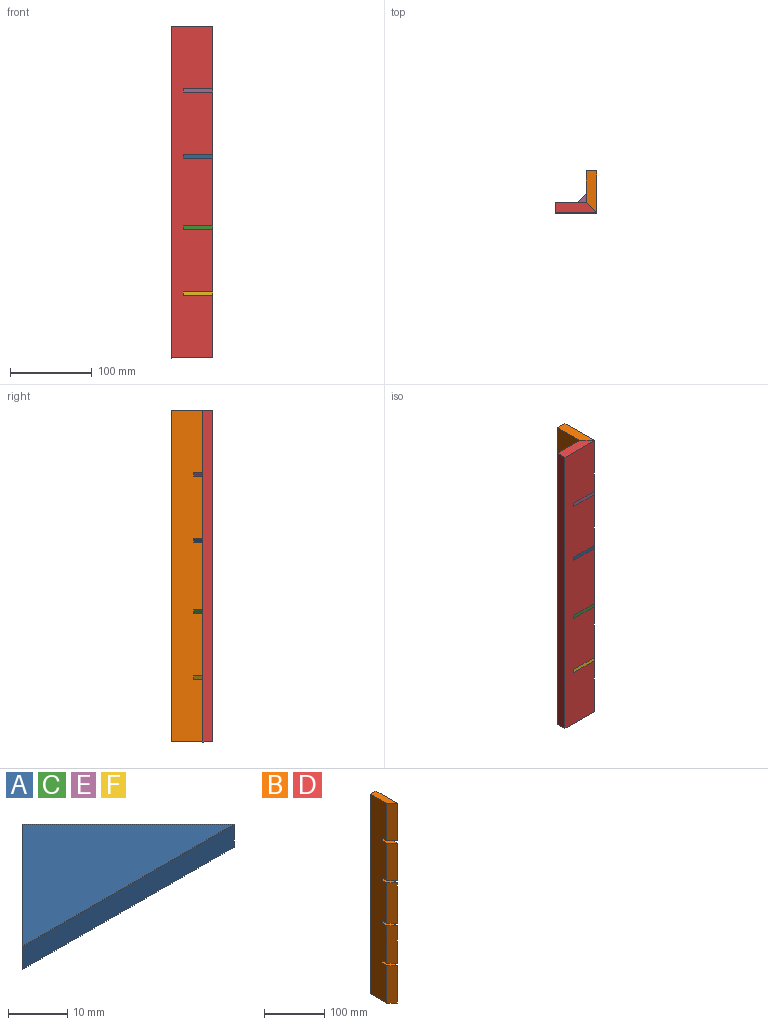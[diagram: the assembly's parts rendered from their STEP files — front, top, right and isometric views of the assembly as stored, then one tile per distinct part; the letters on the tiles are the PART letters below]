
ASSEMBLY  parts=6 mates=8
PART A: 5 faces, bbox 50.8x25.4x4.8 mm
  f0: plane 25.4x25.4mm, normal (-0.71,0.71,0), area 171.1mm2, adj f1,f2,f3,f4
  f1: plane 50.8x4.76mm, normal (0,-1,0), area 241.9mm2, adj f0,f2,f3,f4
  f2: plane 25.4x25.4mm, normal (0.71,0.71,0), area 171.1mm2, adj f0,f1,f3,f4
  f3: plane 50.8x25.4mm, normal (0,0,1), area 645.2mm2, adj f0,f1,f2
  f4: plane 50.8x25.4mm, normal (0,0,-1), area 645.2mm2, adj f0,f1,f2
PART B: 22 faces, bbox 12.7x50.8x406.4 mm
  f0: plane 76.2x12.7mm, normal (-0.71,-0.71,0), area 1368.6mm2, adj f4,f5,f8,f19
  f1: plane 76.2x12.7mm, normal (-0.71,-0.71,0), area 1368.6mm2, adj f4,f5,f15,f16
  f2: plane 76.2x12.7mm, normal (-0.71,-0.71,0), area 1368.6mm2, adj f4,f5,f9,f18
  f3: plane 82.55x12.7mm, normal (-0.71,-0.71,0), area 1482.6mm2, adj f4,f5,f11,f13
  f4: plane 406.4x50.8mm, normal (1,0,0), area 19960.8mm2, adj f0,f1,f2,f3,f6,f7,f8,f9
  f5: plane 406.4x38.1mm, normal (-1,0,0), area 15283.4mm2, adj f0,f1,f2,f3,f6,f7,f8,f9
  f6: plane 76.2x12.7mm, normal (-0.71,-0.71,0), area 1368.6mm2, adj f4,f5,f12,f21
  f7: plane 406.4x12.7mm, normal (0,1,0), area 5161.3mm2, adj f4,f5,f8,f9
  f8: plane 50.8x12.7mm, normal (0,0,1), area 564.5mm2, adj f0,f4,f5,f7
  f9: plane 50.8x12.7mm, normal (0,0,-1), area 564.5mm2, adj f2,f4,f5,f7
  f10: plane 12.7x12.7mm, normal (0.71,-0.71,0), area 85.5mm2, adj f4,f5,f11,f12
  f11: plane 35.92x12.7mm, normal (0,0,1), area 294.9mm2, adj f3,f4,f5,f10
  f12: plane 35.92x12.7mm, normal (0,0,-1), area 294.9mm2, adj f4,f5,f6,f10
  f13: plane 35.92x12.7mm, normal (0,0,-1), area 294.9mm2, adj f3,f4,f5,f14
  f14: plane 12.7x12.7mm, normal (0.71,-0.71,0), area 85.5mm2, adj f4,f5,f13,f15
  f15: plane 35.92x12.7mm, normal (0,0,1), area 294.9mm2, adj f1,f4,f5,f14
  f16: plane 35.92x12.7mm, normal (0,0,-1), area 294.9mm2, adj f1,f4,f5,f17
  f17: plane 12.7x12.7mm, normal (0.71,-0.71,0), area 85.5mm2, adj f4,f5,f16,f18
  f18: plane 35.92x12.7mm, normal (0,0,1), area 294.9mm2, adj f2,f4,f5,f17
  f19: plane 35.92x12.7mm, normal (0,0,-1), area 294.9mm2, adj f0,f4,f5,f20
  f20: plane 12.7x12.7mm, normal (0.71,-0.71,0), area 85.5mm2, adj f4,f5,f19,f21
  f21: plane 35.92x12.7mm, normal (0,0,1), area 294.9mm2, adj f4,f5,f6,f20
PART C: same geometry as A
PART D: same geometry as B
PART E: same geometry as A
PART F: same geometry as A
PLACE A rot(axis=(0.92,0.38,0),180deg) t=(-85.8,196.85,252.71)mm
PLACE B t=(-67.84,178.89,-47.33)mm
PLACE C rot(axis=(0.92,0.38,0),180deg) t=(-85.8,196.85,165.4)mm
PLACE D rot(axis=(-0.71,0.71,0),180deg) t=(-67.84,178.89,460.67)mm
PLACE E rot(axis=(0.92,0.38,0),180deg) t=(-85.8,196.85,333.67)mm
PLACE F rot(axis=(0.92,0.38,0),180deg) t=(-85.8,196.85,84.44)mm
MATE planar D.f9 <-> B.f8  axis (0,0,1) through (-96.27,184.94,409.87)mm
MATE fastened B.f17 <-> F.f1  axis (0.71,-0.71,0) through (-67.84,214.81,84.44)mm
MATE planar B.f3 <-> D.f3  axis (-0.71,-0.71,0) through (-74.19,185.24,206.67)mm
MATE planar B.f20 <-> E.f1  axis (0.71,-0.71,0) through (-74.19,208.46,331.29)mm
MATE planar E.f1 <-> D.f17  axis (-0.71,0.71,0) through (-85.8,196.85,331.29)mm
MATE planar E.f3 <-> B.f21  axis (0,0,-1) through (-79.82,190.87,328.91)mm
MATE planar E.f0 <-> D.f4  axis (0,-1,0) through (-85.8,178.89,331.29)mm
MATE fastened B.f14 <-> C.f1  axis (0.71,-0.71,0) through (-67.84,214.81,165.4)mm
